# Revit family: Haworth_Epure_SingleBench_FixedLegs_AP_PRELIMINARY
name_source: partatom
category: Furniture
units: mm (PartAtom-declared; Revit-internal decimal feet)

## family parameters
Always vertical = Yes
Cut with Voids When Loaded = No
OmniClass Number = 23.40.70.14.64.11
OmniClass Title = Office Furniture
Room Calculation Point = No
Shared = No
Work Plane-Based = No

## types (6) — shared parameters
Actual Height = 730 mm  [stored 2.39501 ft]
Assembly Code = E2020200
Cable Tray Finish = Haworth _ Polymer _ Undecided
Description = Haworth - Epure - Single Bench - Fixed Legs
Flip Top Finish = Haworth _ Paint _ Metallic Silver
Leg Height = 695 mm  [stored 2.28018 ft]
Manufacturer = Haworth
Model = SYEPSBF1XXX
No Accessory Kit = No
Revision Number = 1
Size = Verify Final Dim.w/ Haworth
Trim Finish = Haworth _ Metal _ Structured White EC
URL = https://www.haworth.com
URL - Product = https://www.haworth.com
Warranty = http://www.haworth.com
Worksurface Depth = 600, 700, 750, 800 mm
Worksurface Width = 1200, 1400, 1500, 1600, 1800 mm

## per-type parameters (varying)
| type | Accessory Kit | Actual Depth | Actual Width | Aluminium C | Aluminium L1 | Aluminium L2 | Aluminium Legs | Aluminium R1 | Aluminium R2 | Cable Tray | Cable Tray Width | End Frame | Flip Top Cable Outlet | Intermediary Frame | Round Cable Outlet | Start Frame | Umbilical Cord | Wooden C | Wooden L1 | Wooden L2 | Wooden Legs | Wooden R1 | Wooden R2 |
| 1800 x 800 | Yes | 800 mm  [stored 2.62467 ft] | 1800 mm  [stored 5.90551 ft] | No | No | No | No | No | No | Yes | 1300 mm  [stored 4.26509 ft] | Yes | No | No | Yes | No | Yes | No | Yes | No | Yes | Yes | Yes |
| 1200 x 600 | No | 600 mm | 1200 mm | Yes | Yes | Yes | Yes | Yes | No | Yes | 700 mm | No | No | No | No | Yes | No | No | No | No | No | No | No |
| 1500 x 700 | No | 700 mm | 1500 mm  [stored 4.92126 ft] | No | No | No | No | No | No | Yes | 1000 mm  [stored 3.28084 ft] | No | No | No | No | Yes | No | Yes | Yes | Yes | Yes | Yes | No |
| 1400 x 750 | Yes | 750 mm  [stored 2.46063 ft] | 1400 mm | No | No | No | No | No | No | Yes | 900 mm  [stored 2.95276 ft] | No | Yes | Yes | No | No | No | Yes | Yes | No | Yes | Yes | No |
| 1600 x 750 | No | 750 mm  [stored 2.46063 ft] | 1600 mm | No | No | No | No | No | No | No | 1100 mm | No | Yes | Yes | No | No | Yes | Yes | Yes | No | Yes | Yes | No |
| 1400 x 800 | Yes | 800 mm  [stored 2.62467 ft] | 1400 mm | No | Yes | No | Yes | Yes | Yes | No | 900 mm  [stored 2.95276 ft] | Yes | No | No | Yes | No | Yes | No | No | No | No | No | No |

note: [stored X ft] marks values corroborated as IEEE doubles in the binary element streams (Revit-internal decimal feet)

## geometry (parser evidence)
native form markers: Sweep x30
no freeform markers — native parametric forms only
